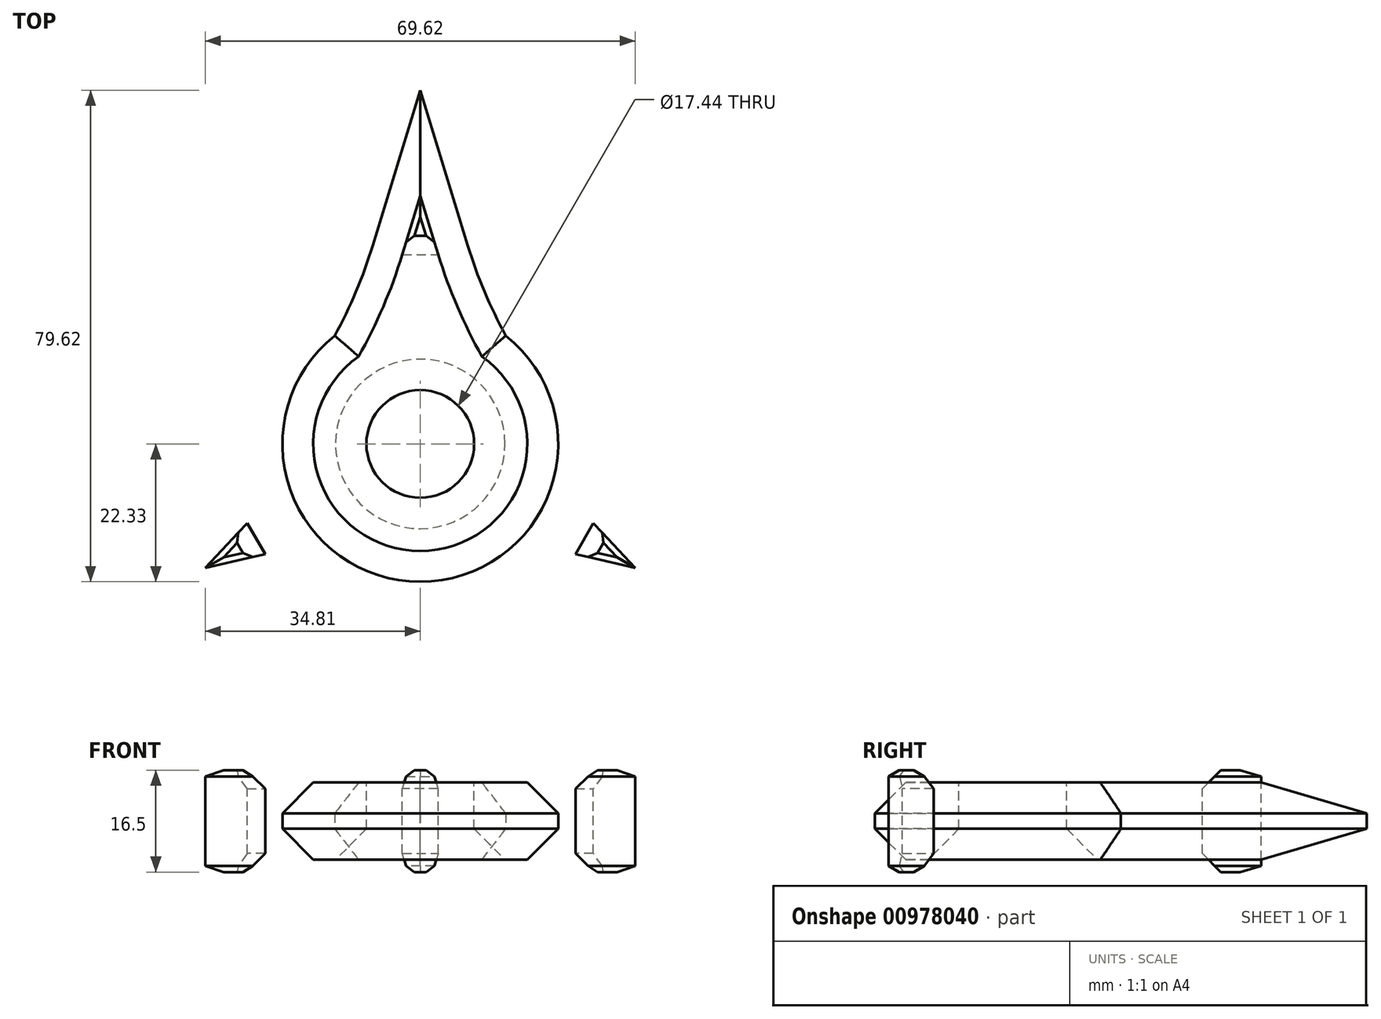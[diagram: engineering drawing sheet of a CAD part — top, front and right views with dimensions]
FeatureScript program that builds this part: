
annotation { "Feature Type Name" : "Feature", "Feature Type Description" : "" }
export const myFeature = defineFeature(function(context is Context, id is Id, definition is map)
    precondition{}
    {
        {
            var Q0;
            Q0=qCreatedBy(makeId("Top.planeOp"),FACE);
            var sketch = newSketch(context, id + "F0", { "sketchPlane" : qUnion([Q0])});
            skArc(sketch, "E0", {"start": v(-13.84, 17.51) * mm, "mid": v(0, -22.33) * mm, "end": v(13.84, 17.51) * mm});
            skPoint(sketch, "E1.middle", {"position": v(0, 22.33) * mm});
            skLineSegment(sketch, "E2", {"start": v(-7.7, 32.14) * mm, "end": v(0, 57.3) * mm});
            skLineSegment(sketch, "E3", {"start": v(0, 57.3) * mm, "end": v(7.7, 32.14) * mm});
            skArc(sketch, "E4", {"start": v(-13.84, 17.51) * mm, "mid": v(-10.4, 24.67) * mm, "end": v(-7.7, 32.14) * mm});
            skArc(sketch, "E5.MirrorCS", {"start": v(13.84, 17.51) * mm, "mid": v(10.4, 24.67) * mm, "end": v(7.7, 32.14) * mm});
            skPoint(sketch, "E1.bottom.start.orphan", {"position": v(7.7, 12.51) * mm});
            skPoint(sketch, "E1.right.start.orphan", {"position": v(-7.7, 12.51) * mm});
            skArc(sketch, "E6.1.0", {"start": v(-22.1, 3.23) * mm, "mid": v(-26.56, -3.33) * mm, "end": v(-31.68, -9.4) * mm});
            skArc(sketch, "E6.1.1", {"start": v(-8.25, -20.75) * mm, "mid": v(-16.17, -21.34) * mm, "end": v(-23.99, -22.73) * mm});
            skLineSegment(sketch, "E6.1.2", {"start": v(-23.99, -22.73) * mm, "end": v(-49.62, -28.65) * mm});
            skLineSegment(sketch, "E6.1.3", {"start": v(-49.62, -28.65) * mm, "end": v(-31.68, -9.4) * mm});
            skArc(sketch, "E6.2.0", {"start": v(8.25, -20.75) * mm, "mid": v(16.17, -21.34) * mm, "end": v(23.99, -22.73) * mm});
            skArc(sketch, "E6.2.1", {"start": v(22.1, 3.23) * mm, "mid": v(26.56, -3.33) * mm, "end": v(31.68, -9.4) * mm});
            skLineSegment(sketch, "E6.2.2", {"start": v(31.68, -9.4) * mm, "end": v(49.62, -28.65) * mm});
            skLineSegment(sketch, "E6.2.3", {"start": v(49.62, -28.65) * mm, "end": v(23.99, -22.73) * mm});
            skSolve(sketch);
        }
        {
            var Q0;
            {var subQ1=sQuery(id+"F0.wireOp",EDGE,"E6.1.0");Q0=makeQuery(id+"F0.imprint","IMPRINT",FACE,{"disambiguationData":[TD([[makeQuery(id+"F0.imprint","IMPRINT",EDGE,{"derivedFrom":subQ1}),1.0]])]});}
            var Q1;
            Q1=makeQuery(id+"F0.imprint","IMPRINT",FACE,{"disambiguationData":[TD([[makeQuery(id+"F0.imprint","IMPRINT",EDGE,{"derivedFrom":sQuery(id+"F0.wireOp",EDGE,"E2")}),-1.0]])]});
            var Q2;
            {var subQ1=sQuery(id+"F0.wireOp",EDGE,"E6.2.0");Q2=makeQuery(id+"F0.imprint","IMPRINT",FACE,{"disambiguationData":[TD([[makeQuery(id+"F0.imprint","IMPRINT",EDGE,{"derivedFrom":subQ1}),1.0]])]});}
            extrude(context, id + "F1", {"entities" : qUnion([Q0, Q1, Q2]), "depth" : 12.5 * mm, "offsetDistance" : 25 * mm});
        }
        {
            var Q0;
            Q0=makeQuery(id+"F1.opExtrude","CAP_FACE",FACE,{"disambiguationData":[OSD([sQuery(id+"F0.wireOp",EDGE,"E0"),sQuery(id+"F0.wireOp",EDGE,"E2"),sQuery(id+"F0.wireOp",EDGE,"E3"),sQuery(id+"F0.wireOp",EDGE,"E4"),sQuery(id+"F0.wireOp",EDGE,"E5.MirrorCS"),sQuery(id+"F0.wireOp",EDGE,"E6.1.0"),sQuery(id+"F0.wireOp",EDGE,"E6.1.1"),sQuery(id+"F0.wireOp",EDGE,"E6.1.2"),sQuery(id+"F0.wireOp",EDGE,"E6.1.3"),sQuery(id+"F0.wireOp",EDGE,"E6.2.0"),sQuery(id+"F0.wireOp",EDGE,"E6.2.1"),sQuery(id+"F0.wireOp",EDGE,"E6.2.2"),sQuery(id+"F0.wireOp",EDGE,"E6.2.3")])],"isStart":false});
            var sketch = newSketch(context, id + "F2", { "sketchPlane" : qUnion([Q0])});
            skCircle(sketch, "E7", {"center": v(0, 0) * mm, "radius": 8.72 * mm});
            skSolve(sketch);
        }
        {
            var Q0;
            Q0=makeQuery(id+"F2.imprint","IMPRINT",FACE,{"disambiguationData":[TD([[makeQuery(id+"F2.imprint","IMPRINT",EDGE,{"derivedFrom":sQuery(id+"F2.wireOp",EDGE,"E7")}),1.0]])]});
            extrude(context, id + "F3", {"entities" : qUnion([Q0]), "operationType" : NewBodyOperationType.REMOVE, "oppositeDirection" : true, "depth" : 25 * mm, "offsetDistance" : 25 * mm});
        }
        {
            var Q0;
            Q0=makeQuery(id+"F1.opExtrude","CAP_EDGE",EDGE,{"disambiguationData":[OSD([sQuery(id+"F0.wireOp",EDGE,"E3")])],"isStart":false});
            var Q1;
            Q1=makeQuery(id+"F1.opExtrude","CAP_EDGE",EDGE,{"disambiguationData":[OSD([sQuery(id+"F0.wireOp",EDGE,"E2")])],"isStart":false});
            var Q2;
            Q2=makeQuery(id+"F1.opExtrude","CAP_EDGE",EDGE,{"disambiguationData":[OSD([sQuery(id+"F0.wireOp",EDGE,"E6.2.2")])],"isStart":false});
            var Q3;
            Q3=makeQuery(id+"F1.opExtrude","CAP_EDGE",EDGE,{"disambiguationData":[OSD([sQuery(id+"F0.wireOp",EDGE,"E6.2.3")])],"isStart":false});
            var Q4;
            Q4=makeQuery(id+"F1.opExtrude","CAP_EDGE",EDGE,{"disambiguationData":[OSD([sQuery(id+"F0.wireOp",EDGE,"E6.1.2")])],"isStart":false});
            var Q5;
            Q5=makeQuery(id+"F1.opExtrude","CAP_EDGE",EDGE,{"disambiguationData":[OSD([sQuery(id+"F0.wireOp",EDGE,"E6.1.3")])],"isStart":false});
            var Q6;
            Q6=makeQuery(id+"F1.opExtrude","CAP_EDGE",EDGE,{"disambiguationData":[OSD([sQuery(id+"F0.wireOp",EDGE,"E6.1.3")])],"isStart":true});
            var Q7;
            Q7=makeQuery(id+"F1.opExtrude","CAP_EDGE",EDGE,{"disambiguationData":[OSD([sQuery(id+"F0.wireOp",EDGE,"E6.1.2")])],"isStart":true});
            var Q8;
            Q8=makeQuery(id+"F1.opExtrude","CAP_EDGE",EDGE,{"disambiguationData":[OSD([sQuery(id+"F0.wireOp",EDGE,"E2")])],"isStart":true});
            var Q9;
            Q9=makeQuery(id+"F1.opExtrude","CAP_EDGE",EDGE,{"disambiguationData":[OSD([sQuery(id+"F0.wireOp",EDGE,"E3")])],"isStart":true});
            var Q10;
            Q10=makeQuery(id+"F1.opExtrude","CAP_EDGE",EDGE,{"disambiguationData":[OSD([sQuery(id+"F0.wireOp",EDGE,"E6.2.2")])],"isStart":true});
            var Q11;
            Q11=makeQuery(id+"F1.opExtrude","CAP_EDGE",EDGE,{"disambiguationData":[OSD([sQuery(id+"F0.wireOp",EDGE,"E6.2.3")])],"isStart":true});
            var Q12;
            {var subQ0=sQuery(id+"F0.wireOp",EDGE,"E0");Q12=makeQuery(id+"F1.opExtrude","CAP_EDGE",EDGE,{"disambiguationData":[OSD([subQ0]),TDD([makeQuery(id+"F0.imprint","IMPRINT",EDGE,{"disambiguationData":[TD([[makeQuery(id+"F0.imprint","INTERSECT",VERTEX,{"derivedFrom":[subQ0,sQuery(id+"F0.wireOp",EDGE,"E6.1.1")]}),-1.0]])],"derivedFrom":subQ0})])],"isStart":true});}
            var Q13;
            {var subQ0=sQuery(id+"F0.wireOp",EDGE,"E0");Q13=makeQuery(id+"F1.opExtrude","CAP_EDGE",EDGE,{"disambiguationData":[OSD([subQ0]),TDD([makeQuery(id+"F0.imprint","IMPRINT",EDGE,{"disambiguationData":[TD([[makeQuery(id+"F0.imprint","INTERSECT",VERTEX,{"derivedFrom":[subQ0,sQuery(id+"F0.wireOp",EDGE,"E4")]}),-1.0]])],"derivedFrom":subQ0})])],"isStart":true});}
            var Q14;
            {var subQ0=sQuery(id+"F0.wireOp",EDGE,"E0");Q14=makeQuery(id+"F1.opExtrude","CAP_EDGE",EDGE,{"disambiguationData":[OSD([subQ0]),TDD([makeQuery(id+"F0.imprint","IMPRINT",EDGE,{"disambiguationData":[TD([[makeQuery(id+"F0.imprint","INTERSECT",VERTEX,{"derivedFrom":[subQ0,sQuery(id+"F0.wireOp",EDGE,"E5.MirrorCS")]}),1.0]])],"derivedFrom":subQ0})])],"isStart":true});}
            var Q15;
            {var subQ0=sQuery(id+"F0.wireOp",EDGE,"E0");Q15=makeQuery(id+"F1.opExtrude","CAP_EDGE",EDGE,{"disambiguationData":[OSD([subQ0]),TDD([makeQuery(id+"F0.imprint","IMPRINT",EDGE,{"disambiguationData":[TD([[makeQuery(id+"F0.imprint","INTERSECT",VERTEX,{"derivedFrom":[subQ0,sQuery(id+"F0.wireOp",EDGE,"E6.1.1")]}),-1.0]])],"derivedFrom":subQ0})])],"isStart":false});}
            var Q16;
            {var subQ0=sQuery(id+"F0.wireOp",EDGE,"E0");Q16=makeQuery(id+"F1.opExtrude","CAP_EDGE",EDGE,{"disambiguationData":[OSD([subQ0]),TDD([makeQuery(id+"F0.imprint","IMPRINT",EDGE,{"disambiguationData":[TD([[makeQuery(id+"F0.imprint","INTERSECT",VERTEX,{"derivedFrom":[subQ0,sQuery(id+"F0.wireOp",EDGE,"E5.MirrorCS")]}),1.0]])],"derivedFrom":subQ0})])],"isStart":false});}
            var Q17;
            {var subQ0=sQuery(id+"F0.wireOp",EDGE,"E0");Q17=makeQuery(id+"F1.opExtrude","CAP_EDGE",EDGE,{"disambiguationData":[OSD([subQ0]),TDD([makeQuery(id+"F0.imprint","IMPRINT",EDGE,{"disambiguationData":[TD([[makeQuery(id+"F0.imprint","INTERSECT",VERTEX,{"derivedFrom":[subQ0,sQuery(id+"F0.wireOp",EDGE,"E4")]}),-1.0]])],"derivedFrom":subQ0})])],"isStart":false});}
            chamfer(context, id + "F4", {"entities" : qUnion([Q0, Q1, Q2, Q3, Q4, Q5, Q6, Q7, Q8, Q9, Q10, Q11, Q12, Q13, Q14, Q15, Q16, Q17]), "width" : 5 * mm, "tangentPropagation" : true});
        }
        {
            var Q0;
            Q0=makeQuery(id+"F1.opExtrude","CAP_FACE",FACE,{"disambiguationData":[OSD([sQuery(id+"F0.wireOp",EDGE,"E0"),sQuery(id+"F0.wireOp",EDGE,"E2"),sQuery(id+"F0.wireOp",EDGE,"E3"),sQuery(id+"F0.wireOp",EDGE,"E4"),sQuery(id+"F0.wireOp",EDGE,"E5.MirrorCS"),sQuery(id+"F0.wireOp",EDGE,"E6.1.0"),sQuery(id+"F0.wireOp",EDGE,"E6.1.1"),sQuery(id+"F0.wireOp",EDGE,"E6.1.2"),sQuery(id+"F0.wireOp",EDGE,"E6.1.3"),sQuery(id+"F0.wireOp",EDGE,"E6.2.0"),sQuery(id+"F0.wireOp",EDGE,"E6.2.1"),sQuery(id+"F0.wireOp",EDGE,"E6.2.2"),sQuery(id+"F0.wireOp",EDGE,"E6.2.3")])],"isStart":true});
            var sketch = newSketch(context, id + "F5", { "sketchPlane" : qUnion([Q0])});
            skLineSegment(sketch, "E8", {"start": v(34.8, 20.1) * mm, "end": v(25.11, 17.86) * mm});
            skLineSegment(sketch, "E9", {"start": v(25.11, 17.86) * mm, "end": v(28.02, 12.82) * mm});
            skLineSegment(sketch, "E10", {"start": v(28.02, 12.82) * mm, "end": v(34.8, 20.1) * mm});
            skPoint(sketch, "E11.endSnap0", {"position": v(16.25, 16.31) * mm});
            skLineSegment(sketch, "E12", {"start": v(22.25, 5.91) * mm, "end": v(28.02, 12.82) * mm});
            skLineSegment(sketch, "E13", {"start": v(25.11, 17.86) * mm, "end": v(16.25, 16.31) * mm});
            skLineSegment(sketch, "E14", {"start": v(16.25, 16.31) * mm, "end": v(22.25, 5.91) * mm});
            skLineSegment(sketch, "E15.1.0", {"start": v(-22.25, 5.91) * mm, "end": v(-16.25, 16.31) * mm});
            skLineSegment(sketch, "E15.1.1", {"start": v(-16.25, 16.31) * mm, "end": v(-25.11, 17.86) * mm});
            skLineSegment(sketch, "E15.1.2", {"start": v(-28.02, 12.82) * mm, "end": v(-25.11, 17.86) * mm});
            skLineSegment(sketch, "E15.1.3", {"start": v(-25.11, 17.86) * mm, "end": v(-34.8, 20.1) * mm});
            skLineSegment(sketch, "E15.1.4", {"start": v(-34.8, 20.1) * mm, "end": v(-28.02, 12.82) * mm});
            skLineSegment(sketch, "E15.1.5", {"start": v(-28.02, 12.82) * mm, "end": v(-22.25, 5.91) * mm});
            skLineSegment(sketch, "E15.2.0", {"start": v(6, -22.23) * mm, "end": v(-6, -22.23) * mm});
            skLineSegment(sketch, "E15.2.1", {"start": v(-6, -22.23) * mm, "end": v(-2.9, -30.68) * mm});
            skLineSegment(sketch, "E15.2.2", {"start": v(2.9, -30.68) * mm, "end": v(-2.9, -30.68) * mm});
            skLineSegment(sketch, "E15.2.3", {"start": v(-2.9, -30.68) * mm, "end": v(0, -40.2) * mm});
            skLineSegment(sketch, "E15.2.4", {"start": v(0, -40.2) * mm, "end": v(2.9, -30.68) * mm});
            skLineSegment(sketch, "E15.2.5", {"start": v(2.9, -30.68) * mm, "end": v(6, -22.23) * mm});
            skPoint(sketch, "E15.center", {"position": v(0, 0) * mm});
            skSolve(sketch);
        }
        {
            var Q0;
            Q0=makeQuery(id+"F5.imprint","IMPRINT",FACE,{"disambiguationData":[TD([[makeQuery(id+"F5.imprint","IMPRINT",EDGE,{"derivedFrom":sQuery(id+"F5.wireOp",EDGE,"E15.1.2")}),1.0]])]});
            var Q1;
            Q1=makeQuery(id+"F5.imprint","IMPRINT",FACE,{"disambiguationData":[TD([[makeQuery(id+"F5.imprint","IMPRINT",EDGE,{"derivedFrom":sQuery(id+"F5.wireOp",EDGE,"E15.2.2")}),1.0]])]});
            var Q2;
            Q2=makeQuery(id+"F5.imprint","IMPRINT",FACE,{"disambiguationData":[TD([[makeQuery(id+"F5.imprint","IMPRINT",EDGE,{"derivedFrom":sQuery(id+"F5.wireOp",EDGE,"E8")}),1.0]])]});
            extrude(context, id + "F6", {"entities" : qUnion([Q0, Q1, Q2]), "depth" : 2 * mm, "offsetDistance" : 25 * mm, "hasSecondDirection" : true, "secondDirectionOppositeDirection" : true, "secondDirectionDepth" : 14.5 * mm});
        }
        {
            var Q0;
            Q0=makeQuery(id+"F6.opExtrude","CAP_EDGE",EDGE,{"disambiguationData":[OSD([sQuery(id+"F5.wireOp",EDGE,"E8")])],"isStart":false});
            var Q1;
            Q1=makeQuery(id+"F6.opExtrude","CAP_EDGE",EDGE,{"disambiguationData":[OSD([sQuery(id+"F5.wireOp",EDGE,"E10")])],"isStart":false});
            var Q2;
            Q2=makeQuery(id+"F6.opExtrude","CAP_EDGE",EDGE,{"disambiguationData":[OSD([sQuery(id+"F5.wireOp",EDGE,"E15.1.3")])],"isStart":false});
            var Q3;
            Q3=makeQuery(id+"F6.opExtrude","CAP_EDGE",EDGE,{"disambiguationData":[OSD([sQuery(id+"F5.wireOp",EDGE,"E15.1.4")])],"isStart":false});
            var Q4;
            Q4=makeQuery(id+"F6.opExtrude","CAP_EDGE",EDGE,{"disambiguationData":[OSD([sQuery(id+"F5.wireOp",EDGE,"E15.2.4")])],"isStart":false});
            var Q5;
            Q5=makeQuery(id+"F6.opExtrude","CAP_EDGE",EDGE,{"disambiguationData":[OSD([sQuery(id+"F5.wireOp",EDGE,"E15.2.3")])],"isStart":false});
            var Q6;
            Q6=makeQuery(id+"F6.opExtrude","CAP_EDGE",EDGE,{"disambiguationData":[OSD([sQuery(id+"F5.wireOp",EDGE,"E10")])],"isStart":true});
            var Q7;
            Q7=makeQuery(id+"F6.opExtrude","CAP_EDGE",EDGE,{"disambiguationData":[OSD([sQuery(id+"F5.wireOp",EDGE,"E8")])],"isStart":true});
            var Q8;
            Q8=makeQuery(id+"F6.opExtrude","CAP_EDGE",EDGE,{"disambiguationData":[OSD([sQuery(id+"F5.wireOp",EDGE,"E15.1.3")])],"isStart":true});
            var Q9;
            {var subQ0=sQuery(id+"F0.wireOp",EDGE,"E6.1.3");Q9=makeQuery(id+"F4.opChamfer","BLEND_EDGE",EDGE,{"blendedFrom":[makeQuery(id+"F1.opExtrude","CAP_EDGE",EDGE,{"disambiguationData":[OSD([subQ0])],"isStart":false}),makeQuery(id+"F1.opExtrude","CAP_FACE",FACE,{"disambiguationData":[OSD([sQuery(id+"F0.wireOp",EDGE,"E0"),sQuery(id+"F0.wireOp",EDGE,"E2"),sQuery(id+"F0.wireOp",EDGE,"E3"),sQuery(id+"F0.wireOp",EDGE,"E4"),sQuery(id+"F0.wireOp",EDGE,"E5.MirrorCS"),sQuery(id+"F0.wireOp",EDGE,"E6.1.0"),sQuery(id+"F0.wireOp",EDGE,"E6.1.1"),sQuery(id+"F0.wireOp",EDGE,"E6.1.2"),subQ0,sQuery(id+"F0.wireOp",EDGE,"E6.2.0"),sQuery(id+"F0.wireOp",EDGE,"E6.2.1"),sQuery(id+"F0.wireOp",EDGE,"E6.2.2"),sQuery(id+"F0.wireOp",EDGE,"E6.2.3")])],"isStart":false})],"blendedInto":[makeQuery(id+"F1.opExtrude","CAP_FACE",FACE,{"disambiguationData":[OSD([sQuery(id+"F0.wireOp",EDGE,"E0"),sQuery(id+"F0.wireOp",EDGE,"E2"),sQuery(id+"F0.wireOp",EDGE,"E3"),sQuery(id+"F0.wireOp",EDGE,"E4"),sQuery(id+"F0.wireOp",EDGE,"E5.MirrorCS"),sQuery(id+"F0.wireOp",EDGE,"E6.1.0"),sQuery(id+"F0.wireOp",EDGE,"E6.1.1"),sQuery(id+"F0.wireOp",EDGE,"E6.1.2"),subQ0,sQuery(id+"F0.wireOp",EDGE,"E6.2.0"),sQuery(id+"F0.wireOp",EDGE,"E6.2.1"),sQuery(id+"F0.wireOp",EDGE,"E6.2.2"),sQuery(id+"F0.wireOp",EDGE,"E6.2.3")])],"isStart":false})]});}
            var Q10;
            Q10=makeQuery(id+"F6.opExtrude","CAP_EDGE",EDGE,{"disambiguationData":[OSD([sQuery(id+"F5.wireOp",EDGE,"E15.2.4")])],"isStart":true});
            var Q11;
            Q11=makeQuery(id+"F6.opExtrude","CAP_EDGE",EDGE,{"disambiguationData":[OSD([sQuery(id+"F5.wireOp",EDGE,"E15.2.3")])],"isStart":true});
            chamfer(context, id + "F7", {"entities" : qUnion([Q0, Q1, Q2, Q3, Q4, Q5, Q6, Q7, Q8, Q9, Q10, Q11]), "width" : 1 * mm, "tangentPropagation" : true});
        }
        {
            var Q0;
            Q0=makeQuery(id+"F6.opExtrude","CAP_EDGE",EDGE,{"disambiguationData":[OSD([sQuery(id+"F5.wireOp",EDGE,"E15.1.4")])],"isStart":true});
            chamfer(context, id + "F8", {"entities" : qUnion([Q0]), "width" : 1 * mm, "tangentPropagation" : true});
        }
        {
            var Q0;
            Q0=makeQuery(id+"F3.boolean.opBoolean","COPY",EDGE,{"derivedFrom":makeQuery(id+"F3.opExtrude","CAP_EDGE",EDGE,{"disambiguationData":[OSD([sQuery(id+"F2.wireOp",EDGE,"E7")])],"isStart":true})});
            var Q1;
            Q1=makeQuery(id+"F3.boolean.opBoolean","INTERSECT",EDGE,{"derivedFrom":[makeQuery(id+"F1.opExtrude","CAP_FACE",FACE,{"disambiguationData":[OSD([sQuery(id+"F0.wireOp",EDGE,"E0"),sQuery(id+"F0.wireOp",EDGE,"E2"),sQuery(id+"F0.wireOp",EDGE,"E3"),sQuery(id+"F0.wireOp",EDGE,"E4"),sQuery(id+"F0.wireOp",EDGE,"E5.MirrorCS"),sQuery(id+"F0.wireOp",EDGE,"E6.1.0"),sQuery(id+"F0.wireOp",EDGE,"E6.1.1"),sQuery(id+"F0.wireOp",EDGE,"E6.1.2"),sQuery(id+"F0.wireOp",EDGE,"E6.1.3"),sQuery(id+"F0.wireOp",EDGE,"E6.2.0"),sQuery(id+"F0.wireOp",EDGE,"E6.2.1"),sQuery(id+"F0.wireOp",EDGE,"E6.2.2"),sQuery(id+"F0.wireOp",EDGE,"E6.2.3")])],"isStart":true}),makeQuery(id+"F3.opExtrude","SWEPT_FACE",FACE,{"disambiguationData":[OSD([sQuery(id+"F2.wireOp",EDGE,"E7")])]})]});
            chamfer(context, id + "F9", {"entities" : qUnion([Q0, Q1]), "width" : 5 * mm, "tangentPropagation" : true});
        }
        {
            var Q0;
            Q0=makeQuery(id+"F6.opExtrude","CAP_EDGE",EDGE,{"disambiguationData":[OSD([sQuery(id+"F5.wireOp",EDGE,"E15.2.2")])],"isStart":false});
            var Q1;
            Q1=makeQuery(id+"F6.opExtrude","CAP_EDGE",EDGE,{"disambiguationData":[OSD([sQuery(id+"F5.wireOp",EDGE,"E15.2.2")])],"isStart":true});
            var Q2;
            Q2=makeQuery(id+"F6.opExtrude","CAP_EDGE",EDGE,{"disambiguationData":[OSD([sQuery(id+"F5.wireOp",EDGE,"E15.1.2")])],"isStart":true});
            var Q3;
            Q3=makeQuery(id+"F6.opExtrude","CAP_EDGE",EDGE,{"disambiguationData":[OSD([sQuery(id+"F5.wireOp",EDGE,"E9")])],"isStart":true});
            var Q4;
            Q4=makeQuery(id+"F6.opExtrude","CAP_EDGE",EDGE,{"disambiguationData":[OSD([sQuery(id+"F5.wireOp",EDGE,"E15.1.2")])],"isStart":false});
            var Q5;
            Q5=makeQuery(id+"F6.opExtrude","CAP_EDGE",EDGE,{"disambiguationData":[OSD([sQuery(id+"F5.wireOp",EDGE,"E9")])],"isStart":false});
            chamfer(context, id + "F10", {"entities" : qUnion([Q0, Q1, Q2, Q3, Q4, Q5]), "width" : 3 * mm, "tangentPropagation" : true});
        }
    });
